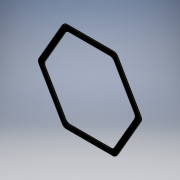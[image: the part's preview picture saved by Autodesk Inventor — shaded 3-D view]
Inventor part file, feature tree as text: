
AUTODESK INVENTOR PART (.ipt)
format: ipt  version: 2019 (Build 230136000, 136)  size: 140,288 bytes
history: native  units: mm
features: extrude x2, fillet x2, sketch x2, projected_geometry x1
ambient origin geometry x8: Origin, YZ Plane, XZ Plane, XY Plane, X Axis, Y Axis, Z Axis, Center Point
bodies: Solid1 (feature_tree)
feature tree (7):
  extrude  "Extrusion1"  Depth=2.0mm TaperAngle=0.0deg
  extrude  "Extrusion6"  Depth=10.0mm
  fillet  "Fillet2"  Radius=10.0mm
  fillet  "Fillet3"  Radius=10.0mm
  sketch  "Sketch1"  dims[d0=175.0mm d1=2.0mm d2=0.0mm]
  sketch  "Sketch7"  dims[d20=7.0mm d21=0.0mm d24=10.0mm d25=10.0mm d26=10.0mm]
  projected_geometry  "Projected Loop7"
